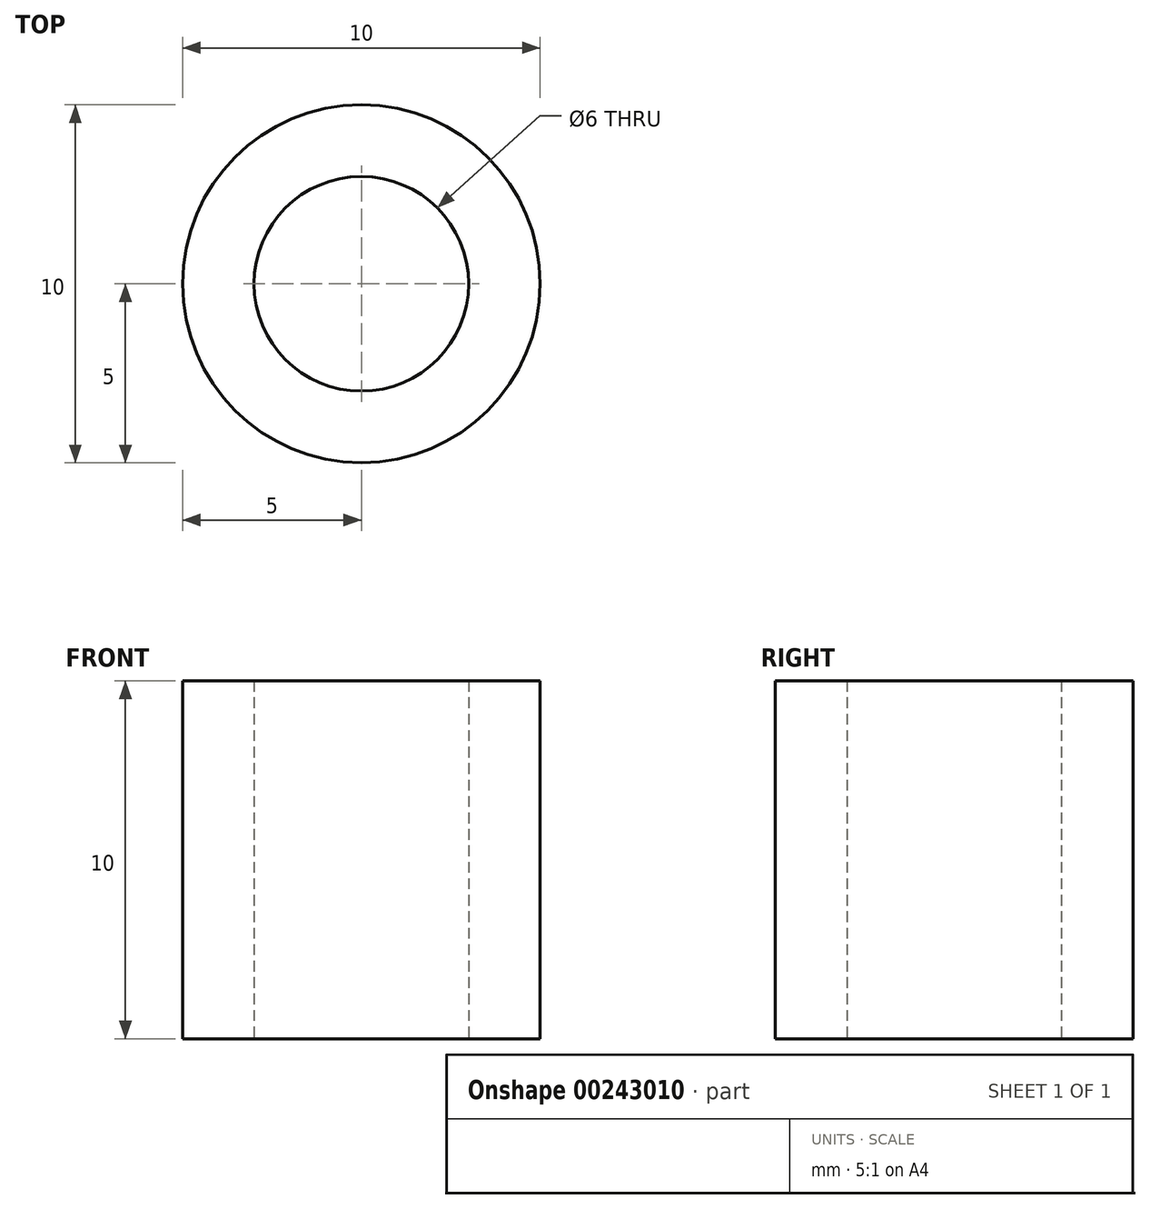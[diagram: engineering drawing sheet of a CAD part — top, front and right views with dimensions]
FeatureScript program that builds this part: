
annotation { "Feature Type Name" : "Feature", "Feature Type Description" : "" }
export const myFeature = defineFeature(function(context is Context, id is Id, definition is map)
    precondition{}
    {
        {
            var Q0;
            Q0=qCreatedBy(makeId("Top.planeOp"),FACE);
            var sketch = newSketch(context, id + "F0", { "sketchPlane" : qUnion([Q0])});
            skCircle(sketch, "E0", {"center": v(0, 0) * mm, "radius": 5 * mm});
            skCircle(sketch, "E1", {"center": v(0, 0) * mm, "radius": 3 * mm});
            skSolve(sketch);
        }
        {
            var Q0;
            Q0 = qSketchRegion(id + "F0", true);
            extrude(context, id + "F1", {"entities" : qUnion([Q0]), "depth" : 10 * mm});
        }
    });
